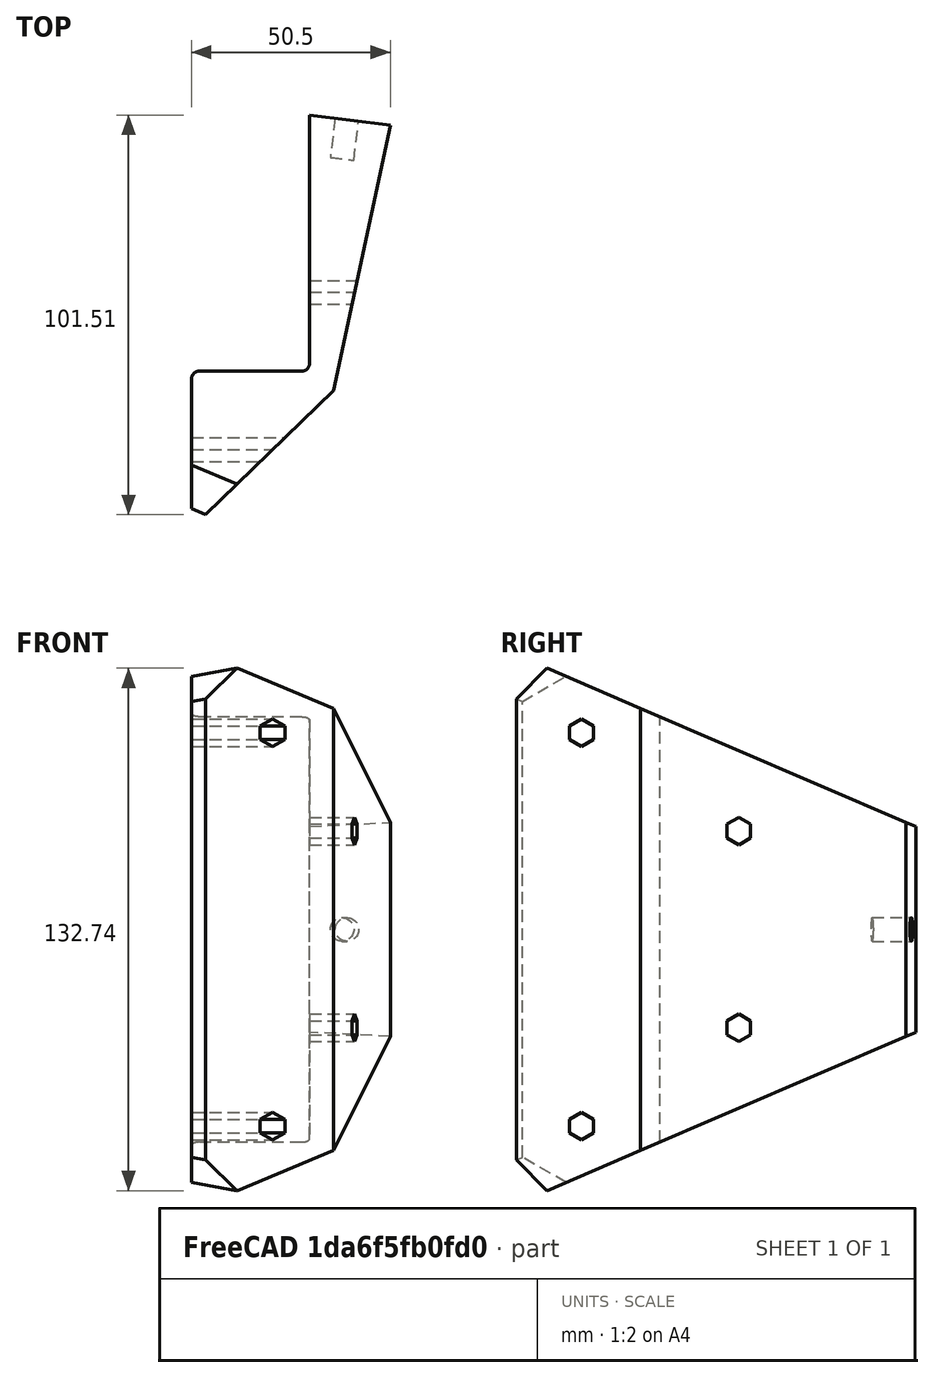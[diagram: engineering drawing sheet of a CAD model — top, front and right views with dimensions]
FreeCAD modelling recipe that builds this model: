
FCSTD DOCUMENT  (FreeCAD 0.19R)
Label: TailLightBracketForRack
License: All rights reserved
LicenseURL: http://en.wikipedia.org/wiki/All_rights_reserved
objects: Sketcher::SketchObject×4, PartDesign::Pocket×3, PartDesign::Chamfer×2, PartDesign::Fillet×2, PartDesign::Pad×1, PartDesign::Body×1, App::Part×1, Mesh::Feature×1
note: 21 computed .brp shape members not serialized (recipe doc carries the construction recipe); baked Part::Feature solids carry a one-line shape summary decoded from their .brp

FEATURE [Sketcher::SketchObject] Sketch007
  FullyConstrained = false
  MapMode = 5
  Support = -> [XY_Plane001]
  sketch-geometry (6):
    g0: LineSegment StartX=6 StartY=0 StartZ=0 EndX=20.4975 EndY=67.4832 EndZ=0
    g1: LineSegment StartX=20.4975 StartY=67.4832 StartZ=0 EndX=0 EndY=70 EndZ=0
    g2: LineSegment StartX=0 StartY=70 StartZ=0 EndX=0 EndY=5 EndZ=0
    g3: LineSegment StartX=-30 StartY=-35 StartZ=0 EndX=-30 EndY=5 EndZ=0
    g4: LineSegment StartX=-30 StartY=5 StartZ=0 EndX=0 EndY=5 EndZ=0
    g5: LineSegment StartX=-30 StartY=-35 StartZ=0 EndX=6 EndY=0 EndZ=0
  constraints (15):
    c: PointOnObject(g0,g-1)
    c: Coincident(g1,g2)
    c: Angle(g1) = 3.01942
    c: Vertical(g3)
    c: Coincident(g3,g4)
    c: Coincident(g4,g2)
    c: Horizontal(g4)
    c: DistanceY(g2) = 5
    c: PointOnObject(g2,g-2)
    c: Distance(g4) = 30
    c: Coincident(g0,g1)
    c: Distance(g3) = 40
    c: Coincident(g5,g3)
    c: Coincident(g5,g0)
    c: DistanceX(g0) = 6
FEATURE [PartDesign::Pad] Pad
  AllowMultiFace = false
  Direction = (1,1,1)
  Length = 140
  Length2 = 100
  Midplane = true
  Profile = -> Sketch007
  Type = 0
FEATURE [Sketcher::SketchObject] Sketch011
  FullyConstrained = true
  MapMode = 5
  Placement = pos=(-30,0,0) rot=(0.57735,-0.57735,-0.57735;2.0944rad)
  Support = -> [Pad]
  sketch-geometry (32):
    g0: Circle CenterX=-25 CenterY=25 CenterZ=0 NormalX=0 NormalY=0 NormalZ=1 AngleXU=0 Radius=3.5
    g1: Circle CenterX=-25 CenterY=-25 CenterZ=0 NormalX=0 NormalY=0 NormalZ=1 AngleXU=0 Radius=3.5
    g2: Circle CenterX=15 CenterY=50 CenterZ=0 NormalX=0 NormalY=0 NormalZ=1 AngleXU=0 Radius=3.5
    g3: Circle CenterX=15 CenterY=-50 CenterZ=0 NormalX=0 NormalY=0 NormalZ=1 AngleXU=0 Radius=3.5
    g4: LineSegment StartX=-25 StartY=21.5 StartZ=0 EndX=-21.9689 EndY=23.25 EndZ=0
    g5: LineSegment StartX=-21.9689 StartY=23.25 StartZ=0 EndX=-21.9689 EndY=26.75 EndZ=0
    g6: LineSegment StartX=-21.9689 StartY=26.75 StartZ=0 EndX=-25 EndY=28.5 EndZ=0
    g7: LineSegment StartX=-25 StartY=28.5 StartZ=0 EndX=-28.0311 EndY=26.75 EndZ=0
    g8: LineSegment StartX=-28.0311 StartY=26.75 StartZ=0 EndX=-28.0311 EndY=23.25 EndZ=0
    g9: LineSegment StartX=-28.0311 StartY=23.25 StartZ=0 EndX=-25 EndY=21.5 EndZ=0
    g10: Circle CenterX=-25 CenterY=25 CenterZ=0 NormalX=0 NormalY=0 NormalZ=1 AngleXU=0 Radius=3.5
    g11: LineSegment StartX=-21.9689 StartY=-26.75 StartZ=0 EndX=-21.9689 EndY=-23.25 EndZ=0
    g12: LineSegment StartX=-21.9689 StartY=-23.25 StartZ=0 EndX=-25 EndY=-21.5 EndZ=0
    g13: LineSegment StartX=-25 StartY=-21.5 StartZ=0 EndX=-28.0311 EndY=-23.25 EndZ=0
    g14: LineSegment StartX=-28.0311 StartY=-23.25 StartZ=0 EndX=-28.0311 EndY=-26.75 EndZ=0
    g15: LineSegment StartX=-28.0311 StartY=-26.75 StartZ=0 EndX=-25 EndY=-28.5 EndZ=0
    g16: LineSegment StartX=-25 StartY=-28.5 StartZ=0 EndX=-21.9689 EndY=-26.75 EndZ=0
    g17: Circle CenterX=-25 CenterY=-25 CenterZ=0 NormalX=0 NormalY=0 NormalZ=1 AngleXU=0 Radius=3.5
    g18: LineSegment StartX=15 StartY=46.5 StartZ=0 EndX=18.0311 EndY=48.25 EndZ=0
    g19: LineSegment StartX=18.0311 StartY=48.25 StartZ=0 EndX=18.0311 EndY=51.75 EndZ=0
    g20: LineSegment StartX=18.0311 StartY=51.75 StartZ=0 EndX=15 EndY=53.5 EndZ=0
    g21: LineSegment StartX=15 StartY=53.5 StartZ=0 EndX=11.9689 EndY=51.75 EndZ=0
    g22: LineSegment StartX=11.9689 StartY=51.75 StartZ=0 EndX=11.9689 EndY=48.25 EndZ=0
    g23: LineSegment StartX=11.9689 StartY=48.25 StartZ=0 EndX=15 EndY=46.5 EndZ=0
    g24: Circle CenterX=15 CenterY=50 CenterZ=0 NormalX=0 NormalY=0 NormalZ=1 AngleXU=0 Radius=3.5
    g25: LineSegment StartX=15 StartY=-53.5 StartZ=0 EndX=18.0311 EndY=-51.75 EndZ=0
    g26: LineSegment StartX=18.0311 StartY=-51.75 StartZ=0 EndX=18.0311 EndY=-48.25 EndZ=0
    g27: LineSegment StartX=18.0311 StartY=-48.25 StartZ=0 EndX=15 EndY=-46.5 EndZ=0
    g28: LineSegment StartX=15 StartY=-46.5 StartZ=0 EndX=11.9689 EndY=-48.25 EndZ=0
    g29: LineSegment StartX=11.9689 StartY=-48.25 StartZ=0 EndX=11.9689 EndY=-51.75 EndZ=0
    g30: LineSegment StartX=11.9689 StartY=-51.75 StartZ=0 EndX=15 EndY=-53.5 EndZ=0
    g31: Circle CenterX=15 CenterY=-50 CenterZ=0 NormalX=0 NormalY=0 NormalZ=1 AngleXU=0 Radius=3.5
  constraints (74):
    c: Symmetric(g3,g2,g-1)
    c: Symmetric(g0,g1,g-1)
    c: Distance(g0,g1) = 50
    c: Distance(g2,g3) = 100
    c: DistanceX(g0) = -25
    c: Equal(g1,g0)
    c: Equal(g1,g2)
    c: Equal(g1,g3)
    c: DistanceX(g2) = 15
    c: Coincident(g4,g5)
    c: Coincident(g5,g6)
    c: Coincident(g6,g7)
    c: Coincident(g7,g8)
    c: Coincident(g8,g9)
    c: Coincident(g9,g4)
    c: Equal(g4, g5-g9) x5
    c: PointOnObject(g4,g10)
    c: PointOnObject(g5,g10)
    c: PointOnObject(g6,g10)
    c: PointOnObject(g7,g10)
    c: PointOnObject(g8,g10)
    c: PointOnObject(g9,g10)
    c: Coincident(g10,g0)
    c: PointOnObject(g9,g0)
    c: Coincident(g11,g12)
    c: Coincident(g12,g13)
    c: Coincident(g13,g14)
    c: Coincident(g14,g15)
    c: Coincident(g15,g16)
    c: Coincident(g16,g11)
    c: Equal(g11, g12-g16) x5
    c: PointOnObject(g11,g17)
    c: PointOnObject(g12,g17)
    c: PointOnObject(g13,g17)
    c: PointOnObject(g14,g17)
    c: PointOnObject(g15,g17)
    c: PointOnObject(g16,g17)
    c: Coincident(g17,g1)
    c: PointOnObject(g16,g1)
    c: Coincident(g18,g19)
    c: Coincident(g19,g20)
    c: Coincident(g20,g21)
    c: Coincident(g21,g22)
    c: Coincident(g22,g23)
    c: Coincident(g23,g18)
    c: Equal(g18, g19-g23) x5
    c: PointOnObject(g18,g24)
    c: PointOnObject(g19,g24)
    c: PointOnObject(g20,g24)
    c: PointOnObject(g21,g24)
    c: PointOnObject(g22,g24)
    c: PointOnObject(g23,g24)
    c: Coincident(g24,g2)
    c: Coincident(g25,g26)
    c: Coincident(g26,g27)
    c: Coincident(g27,g28)
    c: Coincident(g28,g29)
    c: Coincident(g29,g30)
    c: Coincident(g30,g25)
    c: Equal(g25, g26-g30) x5
    c: PointOnObject(g25,g31)
    c: PointOnObject(g26,g31)
    c: PointOnObject(g27,g31)
    c: PointOnObject(g28,g31)
    c: PointOnObject(g29,g31)
    c: PointOnObject(g30,g31)
    c: Coincident(g31,g3)
    c: Diameter(g24) = 7
    c: Diameter(g31) = 7
    c: Diameter(g1) = 7
    c: Vertical(g14)
    c: Vertical(g8)
    c: Vertical(g29)
    c: Vertical(g22)
FEATURE [Sketcher::SketchObject] Sketch012
  FullyConstrained = false
  MapMode = 5
  Placement = pos=(-30,0,0) rot=(0.57735,-0.57735,-0.57735;2.0944rad)
  sketch-geometry (6):
    g0: LineSegment StartX=-78.4416 StartY=22.5 StartZ=0 EndX=62.305 EndY=82.9104 EndZ=0
    g1: LineSegment StartX=62.305 StartY=82.9104 StartZ=0 EndX=-92.0206 EndY=82.9104 EndZ=0
    g2: LineSegment StartX=-92.0206 StartY=82.9104 StartZ=0 EndX=-92.0206 EndY=-82.9104 EndZ=0
    g3: LineSegment StartX=-92.0206 StartY=-82.9104 StartZ=0 EndX=62.305 EndY=-82.9104 EndZ=0
    g4: LineSegment StartX=62.305 StartY=-82.9104 StartZ=0 EndX=-78.4416 EndY=-22.5 EndZ=0
    g5: LineSegment StartX=-78.4416 StartY=-22.5 StartZ=0 EndX=-78.4416 EndY=22.5 EndZ=0
  constraints (12):
    c: Coincident(g0,g1)
    c: Coincident(g1,g2)
    c: Coincident(g2,g3)
    c: Horizontal(g3)
    c: Coincident(g3,g4)
    c: Coincident(g4,g5)
    c: Coincident(g5,g0)
    c: Symmetric(g0,g4,g-1)
    c: Symmetric(g0,g3,g-1)
    c: Distance(g5) = 45
    c: Vertical(g2)
    c: Horizontal(g1)
FEATURE [Sketcher::SketchObject] Sketch013
  FullyConstrained = true
  MapMode = 5
  Placement = pos=(8.46727,68.9604,0) rot=(0.043208,0.706446,0.706446;3.05523rad)
  sketch-geometry (1):
    g0: Circle CenterX=-1 CenterY=0 CenterZ=0 NormalX=0 NormalY=0 NormalZ=1 AngleXU=0 Radius=3
  constraints (3):
    c: PointOnObject(g0,g-1)
    c: Diameter(g0) = 6
    c: DistanceX(g0) = -1
FEATURE [PartDesign::Pocket] Pocket
  BaseFeature = -> Pad
  Length = 5
  Length2 = 100
  Profile = -> Sketch012
  Type = 1
FEATURE [PartDesign::Pocket] Pocket001
  BaseFeature = -> Pocket
  Length = 10
  Length2 = 100
  Profile = -> Sketch013
  Type = 0
FEATURE [PartDesign::Pocket] Pocket002
  BaseFeature = -> Pocket001
  Length = 5
  Length2 = 100
  Profile = -> Sketch011
  Type = 1
FEATURE [PartDesign::Chamfer] Chamfer
  Angle = 45
  Base = -> Pocket002 [Edge2]
  BaseFeature = -> Pocket002
  ChamferType = 0
  FlipDirection = false
  Size = 5
  Size2 = 1
  SupportTransform = false
FEATURE [PartDesign::Fillet] Fillet
  Base = -> Chamfer [Edge68]
  BaseFeature = -> Chamfer
  Radius = 2
  SupportTransform = false
FEATURE [PartDesign::Fillet] Fillet001
  Base = -> Fillet [Edge10]
  BaseFeature = -> Fillet
  Radius = 2
  SupportTransform = false
FEATURE [PartDesign::Chamfer] Chamfer001
  Angle = 45
  Base = -> Fillet001 [Edge6,Edge46]
  BaseFeature = -> Fillet001
  ChamferType = 0
  FlipDirection = false
  Size = 11
  Size2 = 1
  SupportTransform = false
FEATURE [PartDesign::Body] PadBody
  Group = -> [Sketch007,Pad,Sketch011,Sketch012,Sketch013,Pocket,Pocket001,Pocket002,Chamfer,Fillet,Fillet001,Chamfer001]
  Origin = -> Origin001
  Tip = -> Chamfer001
FEATURE [App::Part] Part
  Group = -> [PadBody]
  Origin = -> Origin
FEATURE [Mesh::Feature] Mesh  label="Chamfer001 (Meshed)"
